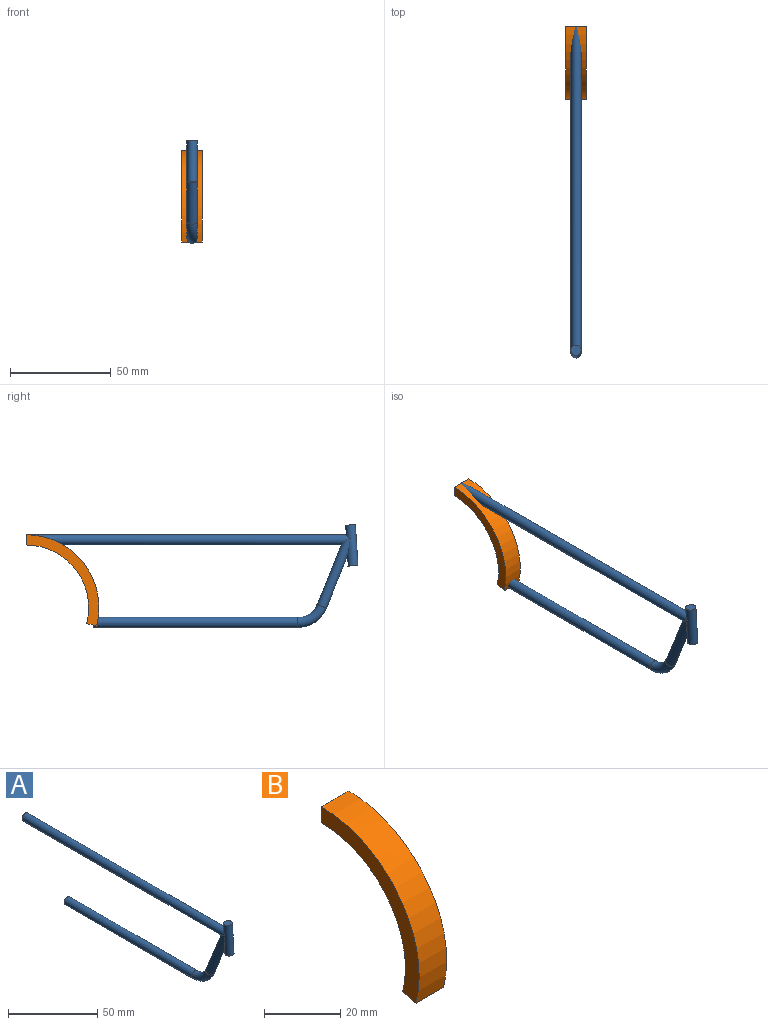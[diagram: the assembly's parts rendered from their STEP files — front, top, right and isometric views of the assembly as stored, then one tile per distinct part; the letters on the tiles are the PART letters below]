
ASSEMBLY  parts=2 mates=1
PART A: 9 faces, bbox 5.1x164.8x52.3 mm
  f0: plane 5.08x5.08mm, normal (0,1,0), area 20.3mm2, adj f2
  f1: plane 5.08x5.08mm, normal (0,1,0), area 20.3mm2, adj f3
  f2: cylinder r=2.54mm len=160.82mm, axis (0,1,0), area 2531.2mm2, adj f0,f5,f8
  f3: cylinder r=2.54mm len=101.6mm, axis (0,-1,0), area 1621.5mm2, adj f1,f4
  f4: torus R=12.69mm, axis (-1,0,0), area 240.6mm2, adj f3,f5
  f5: cylinder r=2.54mm len=35.63mm, axis (0,-0.37,0.93), area 515.4mm2, adj f2,f4,f8
  f6: plane 5.08x5.07mm, normal (0,0.06,1), area 20.3mm2, adj f8
  f7: plane 5.08x5.07mm, normal (0,-0.06,-1), area 20.3mm2, adj f8
  f8: cylinder r=2.54mm len=20.6mm, axis (0,-0.06,-1), area 276mm2, adj f2,f5,f6,f7
PART B: 6 faces, bbox 10.2x36.2x45.3 mm
  f0: plane 10.16x5.08mm, normal (0,1,0), area 51.6mm2, adj f2,f3,f4,f5
  f1: plane 10.16x4.92mm, normal (0,0.25,-0.97), area 51.6mm2, adj f2,f3,f4,f5
  f2: cylinder r=31.11mm len=38.97mm, axis (1,0,0), area 577.2mm2, adj f0,f1,f3,f5
  f3: plane 45.33x36.19mm, normal (1,0,0), area 312.2mm2, adj f0,f1,f2,f4
  f4: cylinder r=36.19mm len=45.33mm, axis (1,0,0), area 671.4mm2, adj f0,f1,f3,f5
  f5: plane 45.33x36.19mm, normal (-1,0,0), area 312.2mm2, adj f0,f1,f2,f4
PLACE A t=(-0.15,6.36,15.82)mm
PLACE B t=(-0.12,58.87,4.89)mm
MATE fastened B.f0 <-> A.f2  axis (0,1,0) through (-0.15,81.96,20.7)mm
